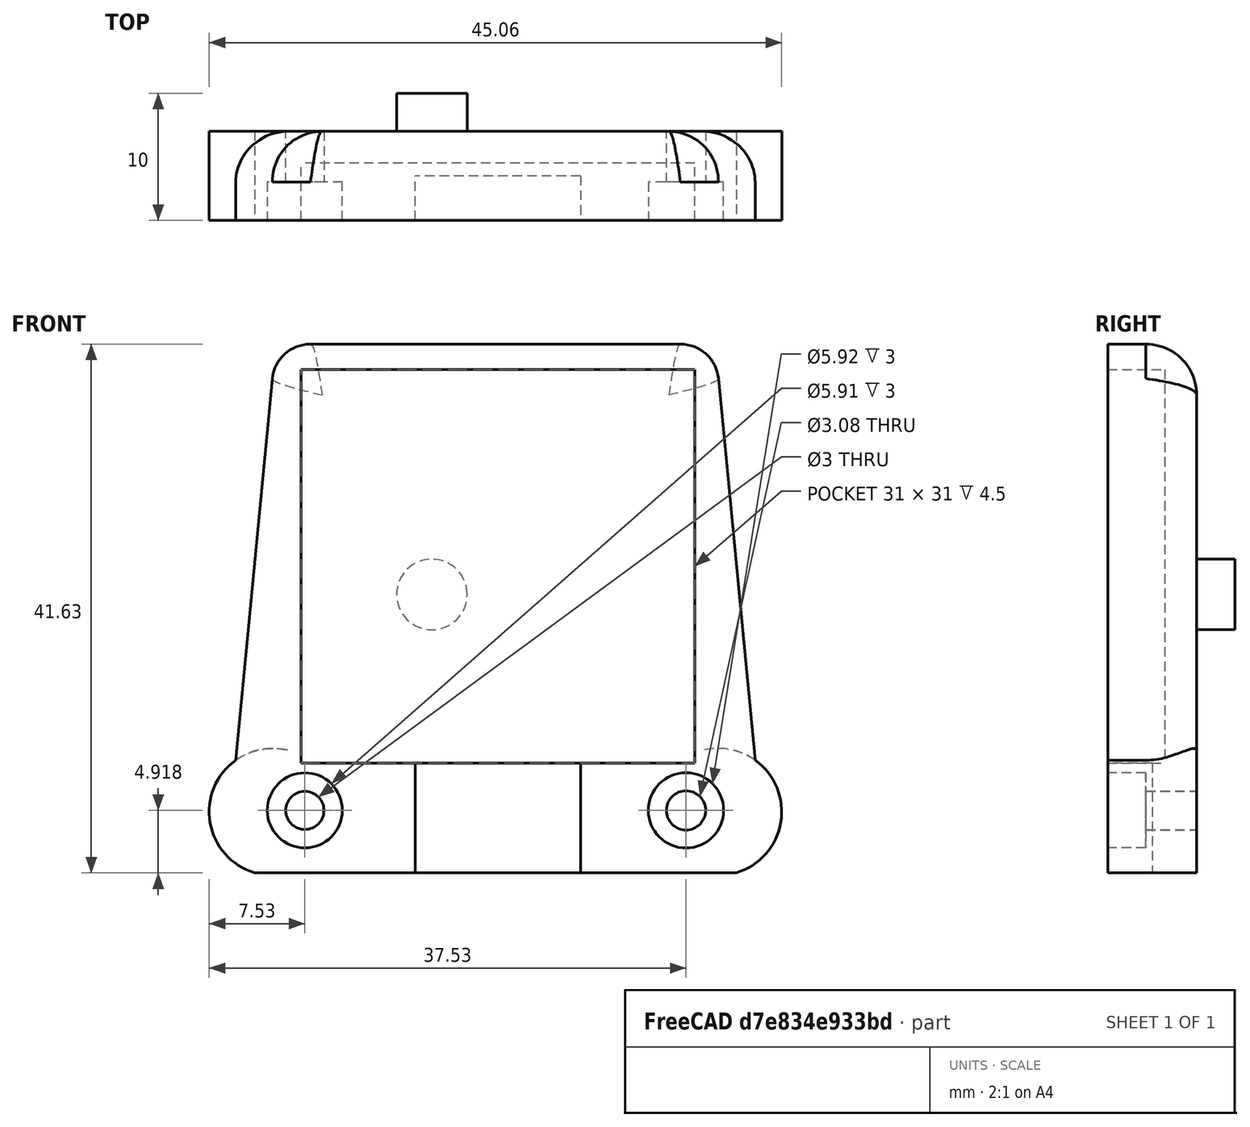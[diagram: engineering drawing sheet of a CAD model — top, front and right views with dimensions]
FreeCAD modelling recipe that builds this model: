
FCSTD DOCUMENT  (FreeCAD 0.17R13519 (Git))
Label: portaGPSinav3
License: All rights reserved
LicenseURL: http://it.wikipedia.org/wiki/<copyright redacted>
objects: Sketcher::SketchObject×5, PartDesign::Pocket×3, PartDesign::Pad×2, PartDesign::Fillet×2, Mesh::Feature×1, PartDesign::Body×1
note: 18 computed .brp shape members not serialized (recipe doc carries the construction recipe); baked Part::Feature solids carry a one-line shape summary decoded from their .brp

FEATURE [Mesh::Feature] ls210_sup
FEATURE [Sketcher::SketchObject] Sketch
  MapMode = 5
  Placement = pos=(0,0,0) rot=(1,0,0;1.5708rad)
  Support = -> [XZ_Plane]
  sketch-geometry (9):
    g0: ArcOfCircle CenterX=5.62653 CenterY=144.818 CenterZ=0 NormalX=0 NormalY=0 NormalZ=1 AngleXU=0 Radius=5 StartAngle=2.19197 EndAngle=4.42446
    g1: ArcOfCircle CenterX=40.6928 CenterY=144.818 CenterZ=0 NormalX=0 NormalY=0 NormalZ=1 AngleXU=0 Radius=5 StartAngle=5.00032 EndAngle=7.23281
    g2: LineSegment StartX=4.20669 StartY=140.024 StartZ=0 EndX=42.1127 EndY=140.024 EndZ=0
    g3: LineSegment StartX=2.7166 StartY=148.884 StartZ=0 EndX=5.87198 EndY=181.653 EndZ=0
    g4: LineSegment StartX=5.87198 StartY=181.653 StartZ=0 EndX=40.4474 EndY=181.653 EndZ=0
    g5: LineSegment StartX=40.4474 StartY=181.653 StartZ=0 EndX=43.6028 EndY=148.884 EndZ=0
    g6: LineSegment [constr] StartX=23.1597 StartY=134.141 StartZ=0 EndX=23.1597 EndY=178.285 EndZ=0
    g7: Circle CenterX=8.15968 CenterY=144.938 CenterZ=0 NormalX=0 NormalY=0 NormalZ=1 AngleXU=0 Radius=1.50187
    g8: Circle CenterX=38.1597 CenterY=144.938 CenterZ=0 NormalX=0 NormalY=0 NormalZ=1 AngleXU=0 Radius=1.54191
  constraints (16):
    c: Coincident(g0,g2)
    c: Coincident(g1,g2)
    c: Coincident(g4,g5)
    c: Horizontal(g2)
    c: Coincident(g5,g1)
    c: Radius(g0) = 5
    c: Equal(g0,g1)
    c: Symmetric(g0,g1,g6)
    c: Horizontal(g4)
    c: Coincident(g3,g0)
    c: Symmetric(g4,g4,g6)
    c: Coincident(g3,g4)
    c: Block(g6)
    c: DistanceX(g7,g8) = 30
    c: Symmetric(g7,g8,g6)
    c: Symmetric(g0,g1,g6)
FEATURE [PartDesign::Pad] Pad
  Length = 7
  Length2 = 100
  Placement = pos=(0,0,0) rot=(1,0,0;1.5708rad)
  Profile = -> Sketch
  Type = 0
FEATURE [Sketcher::SketchObject] Sketch001
  ExternalGeometry = -> [Pad]
  MapMode = 5
  Placement = pos=(0,-7,-1e-12) rot=(1,0,0;1.5708rad)
  Support = -> [Pad]
  sketch-geometry (2):
    g0: Circle CenterX=8.15968 CenterY=144.938 CenterZ=0 NormalX=0 NormalY=0 NormalZ=1 AngleXU=0 Radius=2.95467
    g1: Circle CenterX=38.1597 CenterY=144.938 CenterZ=0 NormalX=0 NormalY=0 NormalZ=1 AngleXU=0 Radius=2.96043
  constraints (2):
    c: Coincident(g-3,g0)
    c: Coincident(g-4,g1)
FEATURE [PartDesign::Pocket] Pocket
  BaseFeature = -> Pad
  Length = 3
  Length2 = 100
  Placement = pos=(0,0,0) rot=(1,0,0;1.5708rad)
  Profile = -> Sketch001
  Type = 0
FEATURE [Sketcher::SketchObject] Sketch002
  ExternalGeometry = -> [Pocket]
  MapMode = 5
  Placement = pos=(0,0,0) rot=(-1,0,0;1.5708rad)
  Support = -> [Pocket]
  sketch-geometry (3):
    g0: Circle CenterX=18.1597 CenterY=-161.938 CenterZ=0 NormalX=0 NormalY=0 NormalZ=1 AngleXU=0 Radius=2.77759
    g1: LineSegment [constr] StartX=8.15968 StartY=-144.938 StartZ=0 EndX=8.15968 EndY=-161.938 EndZ=0
    g2: LineSegment [constr] StartX=18.1597 StartY=-161.938 StartZ=0 EndX=8.15968 EndY=-161.938 EndZ=0
  constraints (7):
    c: Coincident(g0,g2)
    c: Coincident(g1,g2)
    c: Coincident(g-3,g1)
    c: Vertical(g1)
    c: Horizontal(g2)
    c: DistanceY(g1,g1) = 17
    c: DistanceX(g2,g2) = 10
FEATURE [PartDesign::Pad] Pad001
  BaseFeature = -> Pocket
  Length = 3
  Length2 = 100
  Placement = pos=(0,0,0) rot=(1,0,0;1.5708rad)
  Profile = -> Sketch002
  Type = 0
FEATURE [PartDesign::Fillet] Fillet
  Base = -> Pad001 [Edge22,Edge5]
  BaseFeature = -> Pad001
  Placement = pos=(0,0,0) rot=(1,0,0;1.5708rad)
  Radius = 3
FEATURE [PartDesign::Fillet] Fillet001
  Base = -> Fillet [Edge11,Edge9,Edge7,Edge5,Edge1]
  BaseFeature = -> Fillet
  Placement = pos=(0,0,0) rot=(1,0,0;1.5708rad)
  Radius = 4
FEATURE [Sketcher::SketchObject] Sketch003
  MapMode = 5
  Placement = pos=(0,-7,-1e-12) rot=(1,0,0;1.5708rad)
  Support = -> [Pad]
  sketch-geometry (4):
    g0: LineSegment StartX=7.86228 StartY=179.649 StartZ=0 EndX=38.8623 EndY=179.649 EndZ=0
    g1: LineSegment StartX=38.8623 StartY=179.649 StartZ=0 EndX=38.8623 EndY=148.649 EndZ=0
    g2: LineSegment StartX=38.8623 StartY=148.649 StartZ=0 EndX=7.86228 EndY=148.649 EndZ=0
    g3: LineSegment StartX=7.86228 StartY=148.649 StartZ=0 EndX=7.86228 EndY=179.649 EndZ=0
  constraints (10):
    c: Coincident(g0,g1)
    c: Coincident(g1,g2)
    c: Coincident(g2,g3)
    c: Coincident(g3,g0)
    c: Horizontal(g0)
    c: Horizontal(g2)
    c: Vertical(g1)
    c: Vertical(g3)
    c: DistanceX(g0,g0) = 31
    c: DistanceY(g3,g3) = 31
FEATURE [PartDesign::Pocket] Pocket001
  BaseFeature = -> Fillet001
  Length = 4.5
  Length2 = 100
  Placement = pos=(0,0,0) rot=(1,0,0;1.5708rad)
  Profile = -> Sketch003
  Type = 0
FEATURE [Sketcher::SketchObject] Sketch004
  ExternalGeometry = -> [Pocket001]
  MapMode = 5
  Placement = pos=(0,-7,-1e-12) rot=(1,0,0;1.5708rad)
  Support = -> [Pocket001]
  sketch-geometry (4):
    g0: LineSegment StartX=16.8623 StartY=148.953 StartZ=0 EndX=29.8623 EndY=148.953 EndZ=0
    g1: LineSegment StartX=29.8623 StartY=148.953 StartZ=0 EndX=29.8623 EndY=139.772 EndZ=0
    g2: LineSegment StartX=29.8623 StartY=139.772 StartZ=0 EndX=16.8623 EndY=139.772 EndZ=0
    g3: LineSegment StartX=16.8623 StartY=139.772 StartZ=0 EndX=16.8623 EndY=148.953 EndZ=0
  constraints (10):
    c: Coincident(g0,g1)
    c: Coincident(g1,g2)
    c: Coincident(g2,g3)
    c: Coincident(g3,g0)
    c: Horizontal(g0)
    c: Horizontal(g2)
    c: Vertical(g1)
    c: Vertical(g3)
    c: DistanceX(g0,g-3) = 9
    c: DistanceX(g-3,g0) = 9
FEATURE [PartDesign::Pocket] Pocket002
  BaseFeature = -> Pocket001
  Length = 3.5
  Length2 = 100
  Placement = pos=(0,0,0) rot=(1,0,0;1.5708rad)
  Profile = -> Sketch004
  Type = 0
FEATURE [PartDesign::Body] Body
  Group = -> [Sketch,Pad,Sketch001,Pocket,Sketch002,Pad001,Fillet,Fillet001,Sketch003,Pocket001,Sketch004,Pocket002]
  Origin = -> Origin
  Tip = -> Pocket002
